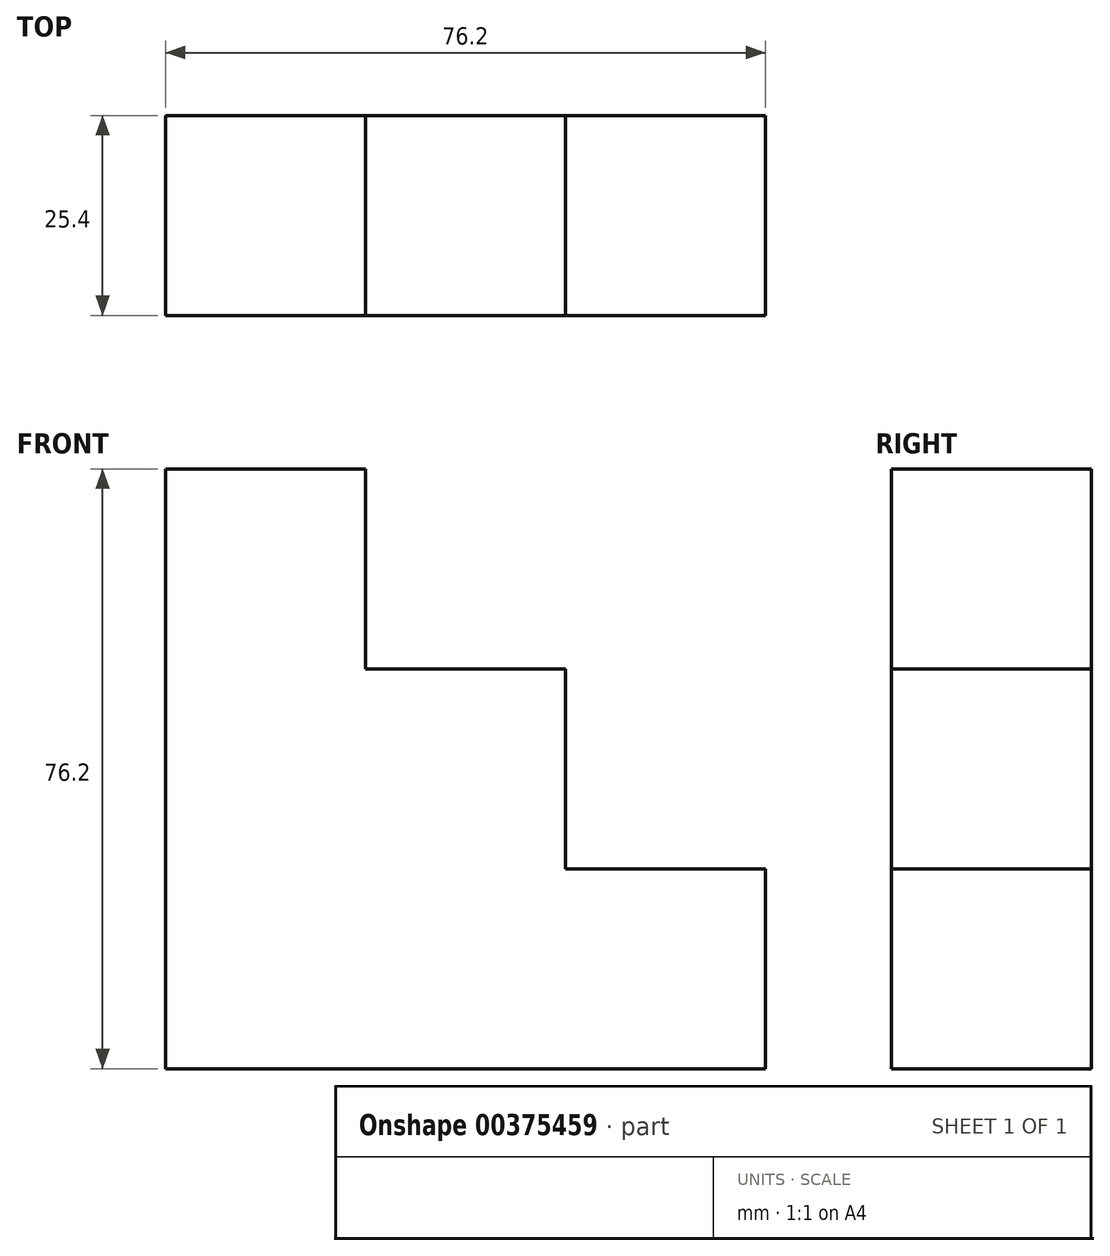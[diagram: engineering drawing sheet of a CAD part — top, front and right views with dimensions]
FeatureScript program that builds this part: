
annotation { "Feature Type Name" : "Feature", "Feature Type Description" : "" }
export const myFeature = defineFeature(function(context is Context, id is Id, definition is map)
    precondition{}
    {
        {
            var Q0;
            Q0=qCreatedBy(makeId("Front.planeOp"),FACE);
            var sketch = newSketch(context, id + "F0", { "sketchPlane" : qUnion([Q0])});
            skLineSegment(sketch, "E0.bottom", {"start": v(0, 0) * mm, "end": v(-25.4, 0) * mm});
            skLineSegment(sketch, "E0.top", {"start": v(0, 25.4) * mm, "end": v(-25.4, 25.4) * mm});
            skLineSegment(sketch, "E0.left", {"start": v(0, 0) * mm, "end": v(0, 25.4) * mm});
            skLineSegment(sketch, "E0.right", {"start": v(-25.4, 0) * mm, "end": v(-25.4, 25.4) * mm});
            skLineSegment(sketch, "E1.bottom", {"start": v(-25.4, 25.4) * mm, "end": v(0, 25.4) * mm});
            skLineSegment(sketch, "E1.top", {"start": v(-25.4, 50.8) * mm, "end": v(0, 50.8) * mm});
            skLineSegment(sketch, "E1.left", {"start": v(-25.4, 25.4) * mm, "end": v(-25.4, 50.8) * mm});
            skLineSegment(sketch, "E1.right", {"start": v(0, 25.4) * mm, "end": v(0, 50.8) * mm});
            skLineSegment(sketch, "E2.top", {"start": v(-25.4, 76.2) * mm, "end": v(0, 76.2) * mm});
            skLineSegment(sketch, "E2.left", {"start": v(-25.4, 50.8) * mm, "end": v(-25.4, 76.2) * mm});
            skLineSegment(sketch, "E2.right", {"start": v(0, 50.8) * mm, "end": v(0, 76.2) * mm});
            skLineSegment(sketch, "E3.bottom", {"start": v(0, 50.8) * mm, "end": v(25.4, 50.8) * mm});
            skLineSegment(sketch, "E3.top", {"start": v(0, 0) * mm, "end": v(25.4, 0) * mm});
            skLineSegment(sketch, "E3.left", {"start": v(0, 50.8) * mm, "end": v(0, 0) * mm});
            skLineSegment(sketch, "E3.right", {"start": v(25.4, 50.8) * mm, "end": v(25.4, 0) * mm});
            skLineSegment(sketch, "E4.bottom", {"start": v(0, 25.4) * mm, "end": v(25.4, 25.4) * mm});
            skLineSegment(sketch, "E4.top", {"start": v(0, 25.4) * mm, "end": v(25.4, 25.4) * mm});
            skLineSegment(sketch, "E4.left", {"start": v(0, 25.4) * mm, "end": v(0, 25.4) * mm});
            skLineSegment(sketch, "E4.right", {"start": v(25.4, 25.4) * mm, "end": v(25.4, 25.4) * mm});
            skLineSegment(sketch, "E5.bottom", {"start": v(25.4, 25.4) * mm, "end": v(50.8, 25.4) * mm});
            skLineSegment(sketch, "E5.top", {"start": v(25.4, 0) * mm, "end": v(50.8, 0) * mm});
            skLineSegment(sketch, "E5.left", {"start": v(25.4, 25.4) * mm, "end": v(25.4, 0) * mm});
            skLineSegment(sketch, "E5.right", {"start": v(50.8, 25.4) * mm, "end": v(50.8, 0) * mm});
            skSolve(sketch);
        }
        {
            var Q0;
            Q0 = qSketchRegion(id + "F0", true);
            extrude(context, id + "F1", {"entities" : qUnion([Q0]), "offsetDistance" : 25.4 * mm, "depth" : 25.4 * mm});
        }
    });
